annotation { "Feature Type Name" : "Feature", "Feature Type Description" : "" }
export const myFeature = defineFeature(function(context is Context, id is Id, definition is map)
    precondition{}
    {
        {
            var Q0;
            Q0=qCreatedBy(makeId("Front.planeOp"),FACE);
            var sketch = newSketch(context, id + "F0", { "sketchPlane" : qUnion([Q0])});
            skLineSegment(sketch, "E0.bottom", {"start": v(-37.24, 68.03) * mm, "end": v(38.96, 68.03) * mm});
            skLineSegment(sketch, "E0.top", {"start": v(-37.24, -46.27) * mm, "end": v(38.96, -46.27) * mm});
            skLineSegment(sketch, "E0.left", {"start": v(-37.24, 68.03) * mm, "end": v(-37.24, -46.27) * mm});
            skLineSegment(sketch, "E0.right", {"start": v(38.96, 68.03) * mm, "end": v(38.96, -46.27) * mm});
            skCircle(sketch, "E1", {"center": v(0, 61.6) * mm, "radius": 3.18 * mm});
            skSolve(sketch);
        }
        {
            var Q0;
            Q0 = qSketchRegion(id + "F0", true);
            extrude(context, id + "F1", {"entities" : qUnion([Q0]), "depth" : 3.17 * mm});
        }
        {
            var Q0;
            Q0=makeQuery(id+"F1.opExtrude","CAP_FACE",FACE,{"disambiguationData":[OSD([sQuery(id+"F0.wireOp",EDGE,"E0.bottom"),sQuery(id+"F0.wireOp",EDGE,"E0.top"),sQuery(id+"F0.wireOp",EDGE,"E0.left"),sQuery(id+"F0.wireOp",EDGE,"E0.right"),sQuery(id+"F0.wireOp",EDGE,"E1")])],"isStart":false});
            var sketch = newSketch(context, id + "F2", { "sketchPlane" : qUnion([Q0])});
            skFitSpline(sketch, "E2", {"points": [v(-30.48, 53.63) * mm, v(-30.48, 53.13) * mm, v(-30.48, 52.34) * mm, v(-30.48, 51.78) * mm, v(-30.67, 51.78) * mm, v(-30.99, 51.82) * mm, v(-31.3, 51.64) * mm, v(-31.49, 51.22) * mm, v(-31.19, 50.58) * mm, v(-30.8, 49.83) * mm, v(-30.6, 49.33) * mm, v(-30.63, 48.52) * mm, v(-30.91, 47.8) * mm, v(-31.24, 47.37) * mm, v(-31.82, 46.99) * mm, v(-32.55, 46.7) * mm, v(-33.63, 46.7) * mm, v(-34.1, 46.85) * mm, v(-34.1, 47.29) * mm, v(-34.09, 48.21) * mm, v(-34.08, 48.74) * mm, v(-33.95, 48.76) * mm, v(-33.62, 48.7) * mm, v(-33.25, 48.76) * mm, v(-32.99, 49.03) * mm, v(-32.94, 49.35) * mm, v(-33.1, 49.69) * mm, v(-33.37, 50.18) * mm, v(-33.58, 50.72) * mm, v(-33.68, 51.1) * mm, v(-33.68, 51.82) * mm, v(-33.67, 52.05) * mm, v(-33.42, 52.52) * mm, v(-33.13, 52.96) * mm, v(-32.7, 53.36) * mm, v(-32.33, 53.64) * mm, v(-31.72, 53.79) * mm, v(-30.93, 53.8) * mm, v(-30.64, 53.75) * mm, v(-30.48, 53.63) * mm]});
            skLineSegment(sketch, "E3", {"start": v(-29.84, 53.68) * mm, "end": v(-29.84, 51.83) * mm});
            skLineSegment(sketch, "E4", {"start": v(-29.84, 51.83) * mm, "end": v(-28.28, 51.83) * mm});
            skLineSegment(sketch, "E5", {"start": v(-28.28, 51.83) * mm, "end": v(-28.28, 46.75) * mm});
            skLineSegment(sketch, "E6", {"start": v(-28.28, 46.75) * mm, "end": v(-26.17, 46.75) * mm});
            skLineSegment(sketch, "E7", {"start": v(-26.17, 46.75) * mm, "end": v(-26.17, 51.71) * mm});
            skLineSegment(sketch, "E8", {"start": v(-24.73, 53.66) * mm, "end": v(-29.84, 53.68) * mm});
            skLineSegment(sketch, "E9", {"start": v(-26.17, 51.71) * mm, "end": v(-26.17, 51.83) * mm});
            skLineSegment(sketch, "E10", {"start": v(-26.17, 51.83) * mm, "end": v(-24.73, 51.83) * mm});
            skLineSegment(sketch, "E11", {"start": v(-24.73, 51.83) * mm, "end": v(-24.73, 53.66) * mm});
            skLineSegment(sketch, "E12", {"start": v(-19.94, 53.7) * mm, "end": v(-19.94, 51.85) * mm});
            skLineSegment(sketch, "E13", {"start": v(-19.94, 51.85) * mm, "end": v(-21.4, 51.85) * mm});
            skLineSegment(sketch, "E14", {"start": v(-21.43, 50.99) * mm, "end": v(-20.1, 50.99) * mm});
            skLineSegment(sketch, "E15", {"start": v(-20.1, 50.99) * mm, "end": v(-20.1, 49.46) * mm});
            skLineSegment(sketch, "E16", {"start": v(-20.1, 49.46) * mm, "end": v(-21.51, 49.46) * mm});
            skLineSegment(sketch, "E17", {"start": v(-21.56, 48.73) * mm, "end": v(-19.94, 48.73) * mm});
            skLineSegment(sketch, "E18", {"start": v(-19.94, 48.73) * mm, "end": v(-19.94, 46.85) * mm});
            skLineSegment(sketch, "E19", {"start": v(-19.94, 46.85) * mm, "end": v(-21.85, 46.85) * mm});
            skLineSegment(sketch, "E20", {"start": v(-19.94, 53.7) * mm, "end": v(-22.07, 53.7) * mm});
            skFitSpline(sketch, "E21", {"points": [v(-22.07, 53.7) * mm, v(-22.34, 53.7) * mm, v(-22.9, 53.47) * mm, v(-23.57, 52.9) * mm, v(-23.85, 52.37) * mm], "startDerivative": vector(-1.48, 0.16) * mm, "endDerivative": vector(-0.8, -2.12) * mm});
            skLineSegment(sketch, "E22", {"start": v(-23.85, 52.37) * mm, "end": v(-23.85, 50.44) * mm});
            skLineSegment(sketch, "E23", {"start": v(-23.85, 50.44) * mm, "end": v(-23.85, 48.3) * mm});
            skFitSpline(sketch, "E24", {"points": [v(-23.85, 48.3) * mm, v(-23.85, 48.05) * mm, v(-23.57, 47.64) * mm, v(-23.22, 47.24) * mm, v(-22.66, 46.9) * mm, v(-21.85, 46.85) * mm], "startDerivative": vector(-0.3, -1.73) * mm, "endDerivative": vector(3.43, 0.14) * mm});
            skLineSegment(sketch, "E25", {"start": v(-22.13, 46.84) * mm, "end": v(-21.85, 46.85) * mm});
            skFitSpline(sketch, "E26", {"points": [v(-21.51, 49.46) * mm, v(-21.7, 49.46) * mm, v(-21.83, 49.33) * mm, v(-21.93, 49.12) * mm, v(-21.8, 48.83) * mm, v(-21.56, 48.73) * mm], "startDerivative": vector(-1.07, 0.16) * mm, "endDerivative": vector(1.22, -0.29) * mm});
            skFitSpline(sketch, "E27", {"points": [v(-21.4, 51.85) * mm, v(-21.56, 51.8) * mm, v(-21.71, 51.73) * mm, v(-21.76, 51.6) * mm, v(-21.78, 51.37) * mm, v(-21.7, 51.2) * mm, v(-21.43, 50.99) * mm], "startDerivative": vector(-1, -0.32) * mm, "endDerivative": vector(1.5, -0.9) * mm});
            skLineSegment(sketch, "E28", {"start": v(-16.5, 51.46) * mm, "end": v(-16.5, 46.84) * mm});
            skLineSegment(sketch, "E29", {"start": v(-16.5, 46.84) * mm, "end": v(-18.54, 46.84) * mm});
            skLineSegment(sketch, "E30", {"start": v(-18.54, 46.84) * mm, "end": v(-18.54, 52.29) * mm});
            skLineSegment(sketch, "E31", {"start": v(-15.91, 51.49) * mm, "end": v(-15.91, 46.86) * mm});
            skLineSegment(sketch, "E32", {"start": v(-15.91, 46.86) * mm, "end": v(-13.89, 46.86) * mm});
            skLineSegment(sketch, "E33", {"start": v(-13.89, 46.86) * mm, "end": v(-13.89, 51.45) * mm});
            skPoint(sketch, "E34.start.orphan", {"position": v(-13.3, 51.45) * mm});
            skLineSegment(sketch, "E35", {"start": v(-13.3, 51.45) * mm, "end": v(-13.3, 46.84) * mm});
            skLineSegment(sketch, "E36", {"start": v(-13.3, 46.84) * mm, "end": v(-11.2, 46.84) * mm});
            skLineSegment(sketch, "E37", {"start": v(-11.2, 46.84) * mm, "end": v(-11.2, 52.1) * mm});
            skFitSpline(sketch, "E38", {"points": [v(-16.5, 51.46) * mm, v(-16.41, 51.6) * mm, v(-16.28, 51.7) * mm, v(-16.1, 51.66) * mm, v(-15.91, 51.49) * mm], "startDerivative": vector(0.3, 0.62) * mm, "endDerivative": vector(0.58, -0.71) * mm});
            skFitSpline(sketch, "E39", {"points": [v(-13.89, 51.45) * mm, v(-13.78, 51.6) * mm, v(-13.66, 51.73) * mm, v(-13.46, 51.7) * mm, v(-13.3, 51.45) * mm], "startDerivative": vector(0.44, 0.67) * mm, "endDerivative": vector(0.48, -0.99) * mm});
            skFitSpline(sketch, "E40", {"points": [v(-18.54, 52.29) * mm, v(-18.54, 52.5) * mm, v(-18.37, 52.81) * mm, v(-18.05, 53.24) * mm, v(-17.56, 53.61) * mm, v(-16.95, 53.81) * mm, v(-16.2, 53.8) * mm, v(-15.26, 53.38) * mm, v(-14.93, 53.04) * mm, v(-14.63, 53.28) * mm, v(-14.24, 53.58) * mm, v(-13.63, 53.8) * mm, v(-12.9, 53.83) * mm, v(-12.14, 53.55) * mm, v(-11.7, 53.19) * mm, v(-11.34, 52.63) * mm, v(-11.2, 52.1) * mm], "startDerivative": vector(-0.69, 5.32) * mm, "endDerivative": vector(1.48, -8.56) * mm});
            skLineSegment(sketch, "E41", {"start": v(-7.27, 51.88) * mm, "end": v(-7.27, 49.15) * mm});
            skLineSegment(sketch, "E42", {"start": v(-7.27, 49.15) * mm, "end": v(-7.27, 46.83) * mm});
            skLineSegment(sketch, "E43", {"start": v(-7.27, 46.83) * mm, "end": v(-5.22, 46.83) * mm});
            skLineSegment(sketch, "E44", {"start": v(-5.22, 46.83) * mm, "end": v(-5.22, 48.36) * mm});
            skLineSegment(sketch, "E45", {"start": v(-5.22, 48.36) * mm, "end": v(-4.7, 48.36) * mm});
            skLineSegment(sketch, "E46", {"start": v(-4.7, 48.36) * mm, "end": v(-4.7, 50.12) * mm});
            skLineSegment(sketch, "E47", {"start": v(-4.7, 50.12) * mm, "end": v(-5.18, 50.12) * mm});
            skLineSegment(sketch, "E48", {"start": v(-5.18, 50.12) * mm, "end": v(-5.18, 51.23) * mm});
            skLineSegment(sketch, "E49", {"start": v(-4.41, 51.45) * mm, "end": v(-4.41, 46.79) * mm});
            skLineSegment(sketch, "E50", {"start": v(-4.41, 46.79) * mm, "end": v(-2.3, 46.79) * mm});
            skLineSegment(sketch, "E51", {"start": v(-2.3, 46.79) * mm, "end": v(-2.3, 51.76) * mm});
            skFitSpline(sketch, "E52", {"points": [v(-5.18, 51.23) * mm, v(-5.18, 51.45) * mm, v(-5.06, 51.6) * mm, v(-4.88, 51.76) * mm, v(-4.62, 51.74) * mm, v(-4.41, 51.63) * mm, v(-4.41, 51.45) * mm], "startDerivative": vector(-0.2, 1.44) * mm, "endDerivative": vector(-0.28, -1.28) * mm});
            skPoint(sketch, "E53.1.internal.orphan", {"position": v(-7.27, 52.16) * mm});
            skFitSpline(sketch, "E54", {"points": [v(-7.27, 51.88) * mm, v(-7.27, 52.16) * mm, v(-7.15, 52.5) * mm, v(-6.93, 52.86) * mm, v(-6.15, 53.5) * mm, v(-5.36, 53.78) * mm, v(-4.25, 53.8) * mm, v(-3.38, 53.4) * mm, v(-2.7, 52.63) * mm, v(-2.3, 51.76) * mm], "startDerivative": vector(-0.36, 4) * mm, "endDerivative": vector(2.73, -7.06) * mm});
            skPoint(sketch, "E55.4.internal.orphan", {"position": v(1.88, 51.74) * mm});
            skPoint(sketch, "E55.5.internal.orphan", {"position": v(0.63, 51.74) * mm});
            skArc(sketch, "E56", {"start": v(3.7, 49.78) * mm, "mid": v(-1.39, 48.98) * mm, "end": v(3.75, 49.16) * mm});
            skArc(sketch, "E57", {"start": v(1.88, 49.76) * mm, "mid": v(0.41, 49.41) * mm, "end": v(1.89, 49.12) * mm});
            skLineSegment(sketch, "E58", {"start": v(1.88, 49.76) * mm, "end": v(3.7, 49.78) * mm});
            skLineSegment(sketch, "E59", {"start": v(3.75, 49.16) * mm, "end": v(1.89, 49.12) * mm});
            skArc(sketch, "E60", {"start": v(9.55, 49.88) * mm, "mid": v(4.75, 50.79) * mm, "end": v(7.47, 46.74) * mm});
            skArc(sketch, "E61", {"start": v(7.63, 49.41) * mm, "mid": v(6.22, 49.35) * mm, "end": v(7.39, 48.55) * mm});
            skLineSegment(sketch, "E62", {"start": v(7.39, 48.55) * mm, "end": v(7.47, 46.74) * mm});
            skLineSegment(sketch, "E63", {"start": v(7.63, 49.41) * mm, "end": v(7.63, 46.74) * mm});
            skLineSegment(sketch, "E64", {"start": v(7.63, 46.74) * mm, "end": v(9.63, 46.74) * mm});
            skLineSegment(sketch, "E65", {"start": v(9.63, 46.74) * mm, "end": v(9.55, 49.88) * mm});
            skArc(sketch, "E66", {"start": v(13.54, 51.72) * mm, "mid": v(11.07, 47.57) * mm, "end": v(15.72, 48.9) * mm});
            skArc(sketch, "E67", {"start": v(13.49, 49.87) * mm, "mid": v(12.42, 48.97) * mm, "end": v(13.81, 49.12) * mm});
            skLineSegment(sketch, "E68", {"start": v(13.54, 51.72) * mm, "end": v(13.49, 49.87) * mm});
            skLineSegment(sketch, "E69", {"start": v(13.81, 49.12) * mm, "end": v(13.81, 53.67) * mm});
            skLineSegment(sketch, "E70", {"start": v(13.81, 53.67) * mm, "end": v(15.69, 53.63) * mm});
            skLineSegment(sketch, "E71", {"start": v(15.69, 53.63) * mm, "end": v(15.72, 48.9) * mm});
            skArc(sketch, "E72", {"start": v(21.73, 49.02) * mm, "mid": v(16.83, 50.38) * mm, "end": v(20.85, 47.26) * mm});
            skLineSegment(sketch, "E73", {"start": v(21.73, 49.02) * mm, "end": v(18.9, 49.02) * mm});
            skLineSegment(sketch, "E74", {"start": v(18.9, 49.02) * mm, "end": v(18.9, 49.76) * mm});
            skLineSegment(sketch, "E75", {"start": v(18.9, 49.76) * mm, "end": v(19.95, 49.76) * mm});
            skLineSegment(sketch, "E76", {"start": v(19.79, 48.5) * mm, "end": v(20.85, 47.26) * mm});
            skFitSpline(sketch, "E77", {"points": [v(19.95, 49.76) * mm, v(19.89, 50.01) * mm, v(19.57, 50.33) * mm, v(19.06, 50.37) * mm, v(18.66, 49.93) * mm, v(18.51, 49.08) * mm, v(18.97, 48.39) * mm, v(19.79, 48.5) * mm], "startDerivative": vector(-0.3, 2.59) * mm, "endDerivative": vector(5.21, 1.83) * mm});
            skLineSegment(sketch, "E78", {"start": v(22.63, 50.3) * mm, "end": v(22.63, 46.84) * mm});
            skLineSegment(sketch, "E79", {"start": v(22.63, 46.84) * mm, "end": v(24.5, 46.84) * mm});
            skLineSegment(sketch, "E80", {"start": v(24.5, 46.84) * mm, "end": v(24.52, 49.49) * mm});
            skArc(sketch, "E81", {"start": v(26.01, 51.12) * mm, "mid": v(24.07, 51.77) * mm, "end": v(22.63, 50.3) * mm});
            skArc(sketch, "E82", {"start": v(29.36, 50.47) * mm, "mid": v(27.9, 51.87) * mm, "end": v(26.01, 51.12) * mm});
            skArc(sketch, "E83", {"start": v(25.08, 49.49) * mm, "mid": v(24.8, 49.9) * mm, "end": v(24.52, 49.49) * mm});
            skArc(sketch, "E84", {"start": v(27.62, 49.49) * mm, "mid": v(27.4, 49.85) * mm, "end": v(27.03, 49.63) * mm});
            skLineSegment(sketch, "E85", {"start": v(25.08, 49.49) * mm, "end": v(25.08, 46.84) * mm});
            skLineSegment(sketch, "E86", {"start": v(25.08, 46.84) * mm, "end": v(27.05, 46.84) * mm});
            skLineSegment(sketch, "E87", {"start": v(27.05, 46.84) * mm, "end": v(27.03, 49.63) * mm});
            skLineSegment(sketch, "E88", {"start": v(29.36, 50.47) * mm, "end": v(29.36, 46.8) * mm});
            skLineSegment(sketch, "E89", {"start": v(29.36, 46.8) * mm, "end": v(27.62, 46.8) * mm});
            skLineSegment(sketch, "E90", {"start": v(27.62, 46.8) * mm, "end": v(27.62, 49.49) * mm});
            skLineSegment(sketch, "E91", {"start": v(30.72, 51.75) * mm, "end": v(32.56, 51.75) * mm});
            skLineSegment(sketch, "E92", {"start": v(32.56, 51.75) * mm, "end": v(32.61, 48.97) * mm});
            skLineSegment(sketch, "E93", {"start": v(30.72, 51.75) * mm, "end": v(30.72, 48.15) * mm});
            skLineSegment(sketch, "E94", {"start": v(33.36, 48.9) * mm, "end": v(33.36, 51.73) * mm});
            skLineSegment(sketch, "E95", {"start": v(33.36, 51.73) * mm, "end": v(35.13, 51.73) * mm});
            skLineSegment(sketch, "E96", {"start": v(35.13, 51.73) * mm, "end": v(35.13, 46.95) * mm});
            skLineSegment(sketch, "E97", {"start": v(31.48, 46.1) * mm, "end": v(31.48, 44.74) * mm});
            skLineSegment(sketch, "E98", {"start": v(31.48, 44.74) * mm, "end": v(31.48, 44.58) * mm});
            skArc(sketch, "E99", {"start": v(32.61, 48.97) * mm, "mid": v(32.95, 48.6) * mm, "end": v(33.36, 48.9) * mm});
            skArc(sketch, "E100", {"start": v(30.72, 48.15) * mm, "mid": v(31.76, 46.92) * mm, "end": v(33.36, 47.08) * mm});
            skFitSpline(sketch, "E101", {"points": [v(33.36, 47.08) * mm, v(33.14, 46.68) * mm, v(32.58, 46.18) * mm, v(32.01, 46.05) * mm, v(31.48, 46.1) * mm], "startDerivative": vector(-0.76, -1.75) * mm, "endDerivative": vector(-2.19, 0.34) * mm});
            skFitSpline(sketch, "E102", {"points": [v(35.13, 46.95) * mm, v(35.13, 46.37) * mm, v(34.85, 45.87) * mm, v(34.16, 45.09) * mm, v(33.65, 44.69) * mm, v(32.75, 44.44) * mm, v(31.48, 44.58) * mm], "startDerivative": vector(0.42, -4.32) * mm, "endDerivative": vector(-6.24, 1.17) * mm});
            skSolve(sketch);
        }
        {
            var Q0;
            Q0=makeQuery(id+"F2.imprint","IMPRINT",FACE,{"disambiguationData":[TD([[makeQuery(id+"F2.imprint","IMPRINT",EDGE,{"derivedFrom":sQuery(id+"F2.wireOp",EDGE,"E2")}),-1.0]])]});
            var Q1;
            Q1=makeQuery(id+"F2.imprint","IMPRINT",FACE,{"disambiguationData":[TD([[makeQuery(id+"F2.imprint","IMPRINT",EDGE,{"derivedFrom":sQuery(id+"F2.wireOp",EDGE,"E3")}),1.0]])]});
            var Q2;
            Q2=makeQuery(id+"F2.imprint","IMPRINT",FACE,{"disambiguationData":[TD([[makeQuery(id+"F2.imprint","IMPRINT",EDGE,{"derivedFrom":sQuery(id+"F2.wireOp",EDGE,"E12")}),-1.0]])]});
            var Q3;
            Q3=makeQuery(id+"F2.imprint","IMPRINT",FACE,{"disambiguationData":[TD([[makeQuery(id+"F2.imprint","IMPRINT",EDGE,{"derivedFrom":sQuery(id+"F2.wireOp",EDGE,"E28")}),-1.0]])]});
            var Q4;
            Q4=makeQuery(id+"F2.imprint","IMPRINT",FACE,{"disambiguationData":[TD([[makeQuery(id+"F2.imprint","IMPRINT",EDGE,{"derivedFrom":sQuery(id+"F2.wireOp",EDGE,"E41")}),1.0]])]});
            var Q5;
            Q5=makeQuery(id+"F2.imprint","IMPRINT",FACE,{"disambiguationData":[TD([[makeQuery(id+"F2.imprint","IMPRINT",EDGE,{"derivedFrom":sQuery(id+"F2.wireOp",EDGE,"E56")}),1.0]])]});
            var Q6;
            Q6=makeQuery(id+"F2.imprint","IMPRINT",FACE,{"disambiguationData":[TD([[makeQuery(id+"F2.imprint","IMPRINT",EDGE,{"derivedFrom":sQuery(id+"F2.wireOp",EDGE,"E60")}),1.0]])]});
            var Q7;
            Q7=makeQuery(id+"F2.imprint","IMPRINT",FACE,{"disambiguationData":[TD([[makeQuery(id+"F2.imprint","IMPRINT",EDGE,{"derivedFrom":sQuery(id+"F2.wireOp",EDGE,"E66")}),1.0]])]});
            var Q8;
            Q8=makeQuery(id+"F2.imprint","IMPRINT",FACE,{"disambiguationData":[TD([[makeQuery(id+"F2.imprint","IMPRINT",EDGE,{"derivedFrom":sQuery(id+"F2.wireOp",EDGE,"E72")}),1.0]])]});
            var Q9;
            Q9=makeQuery(id+"F2.imprint","IMPRINT",FACE,{"disambiguationData":[TD([[makeQuery(id+"F2.imprint","IMPRINT",EDGE,{"derivedFrom":sQuery(id+"F2.wireOp",EDGE,"E78")}),1.0]])]});
            var Q10;
            Q10=makeQuery(id+"F2.imprint","IMPRINT",FACE,{"disambiguationData":[TD([[makeQuery(id+"F2.imprint","IMPRINT",EDGE,{"derivedFrom":sQuery(id+"F2.wireOp",EDGE,"E91")}),-1.0]])]});
            extrude(context, id + "F3", {"entities" : qUnion([Q0, Q1, Q2, Q3, Q4, Q5, Q6, Q7, Q8, Q9, Q10]), "operationType" : NewBodyOperationType.REMOVE, "oppositeDirection" : true, "depth" : 3.17 * mm});
        }
        {
            var Q0;
            Q0=makeQuery(id+"F1.opExtrude","CAP_FACE",FACE,{"disambiguationData":[OSD([sQuery(id+"F0.wireOp",EDGE,"E0.bottom"),sQuery(id+"F0.wireOp",EDGE,"E0.top"),sQuery(id+"F0.wireOp",EDGE,"E0.left"),sQuery(id+"F0.wireOp",EDGE,"E0.right"),sQuery(id+"F0.wireOp",EDGE,"E1")])],"isStart":false});
            var sketch = newSketch(context, id + "F4", { "sketchPlane" : qUnion([Q0])});
            skText(sketch, "E103", { "text": "Hall Pass", "fontName": "NotoSansCJKtc-Bold.otf"});
            const initialGuessF4  = {"E103": [-0.03423, 0.0326, 1, 0, 0.01078]};
            skSetInitialGuess(sketch, initialGuessF4);
            skSolve(sketch);
        }
        {
            var Q0;
            Q0 = qSketchRegion(id + "F4", true);
            extrude(context, id + "F5", {"entities" : qUnion([Q0]), "operationType" : NewBodyOperationType.REMOVE, "oppositeDirection" : true, "depth" : 25.4 * mm});
        }
        {
            var Q0;
            {var subQ0=sQuery(id+"F0.wireOp",EDGE,"E0.left");var subQ1=sQuery(id+"F0.wireOp",EDGE,"E0.top");var subQ2=sQuery(id+"F0.wireOp",EDGE,"E0.right");var subQ3=sQuery(id+"F0.wireOp",EDGE,"E1");var subQ4=sQuery(id+"F0.wireOp",EDGE,"E0.bottom");Q0=makeQuery(id+"F5.boolean.opBoolean","SPLIT",FACE,{"disambiguationData":[TD([makeQuery(id+"F1.opExtrude","SWEPT_FACE",FACE,{"disambiguationData":[OSD([subQ4])]})])],"derivedFrom":makeQuery(id+"F1.opExtrude","CAP_FACE",FACE,{"disambiguationData":[OSD([subQ4,subQ1,subQ0,subQ2,subQ3])],"isStart":false})});}
            var sketch = newSketch(context, id + "F6", { "sketchPlane" : qUnion([Q0])});
            skLineSegment(sketch, "E104", {"start": v(-10.04, 26.02) * mm, "end": v(-14.61, 18.29) * mm});
            skLineSegment(sketch, "E105", {"start": v(-14.61, 18.29) * mm, "end": v(-5.9, 12.73) * mm});
            skLineSegment(sketch, "E106", {"start": v(-5.9, 12.73) * mm, "end": v(0, 21.98) * mm});
            skLineSegment(sketch, "E107", {"start": v(-21.58, 12.4) * mm, "end": v(-11.56, 12.4) * mm});
            skLineSegment(sketch, "E108", {"start": v(-11.56, 12.4) * mm, "end": v(-6.88, 4.02) * mm});
            skLineSegment(sketch, "E109", {"start": v(-6.88, 4.02) * mm, "end": v(-9.27, 5.22) * mm});
            skLineSegment(sketch, "E110", {"start": v(-9.27, 5.22) * mm, "end": v(-13.3, -0.77) * mm});
            skLineSegment(sketch, "E111", {"start": v(-13.3, -0.77) * mm, "end": v(-14.5, -2.52) * mm});
            skLineSegment(sketch, "E112", {"start": v(-21.58, 12.4) * mm, "end": v(-18.75, 10.45) * mm});
            skLineSegment(sketch, "E113", {"start": v(-18.75, 10.45) * mm, "end": v(-21.83, 5.22) * mm});
            skLineSegment(sketch, "E114", {"start": v(-21.83, 5.22) * mm, "end": v(-21.83, 4.02) * mm});
            skLineSegment(sketch, "E115", {"start": v(-21.83, 4.02) * mm, "end": v(-15.7, -7.1) * mm});
            skFitSpline(sketch, "E116", {"points": [v(-14.5, -2.52) * mm, v(-15.2, -4.32) * mm, v(-15.7, -7.1) * mm], "startDerivative": vector(-1.7, -3.73) * mm, "endDerivative": vector(-0.73, -5.37) * mm});
            skPoint(sketch, "E117.3.internal.snap0", {"position": v(-2.95, 17.36) * mm});
            skFitSpline(sketch, "E117", {"points": [v(-10.04, 26.02) * mm, v(-8.51, 27.18) * mm, v(-5.9, 27.6) * mm, v(-2.95, 26.94) * mm, v(-1.25, 24) * mm, v(0, 21.98) * mm], "startDerivative": vector(8.08, 7.85) * mm, "endDerivative": vector(6.8, -9.49) * mm});
            skFitSpline(sketch, "E118", {"points": [v(-11.94, -1.05) * mm, v(-13, -2.52) * mm, v(-14.5, -5.22) * mm, v(-13.82, -8.8) * mm, v(-11.61, -11.1) * mm, v(-10.04, -11.74) * mm], "startDerivative": vector(-5.8, -8.2) * mm, "endDerivative": vector(9.47, -2.91) * mm});
            skLineSegment(sketch, "E119", {"start": v(-11.94, -1.05) * mm, "end": v(-1.09, -1.05) * mm});
            skLineSegment(sketch, "E120", {"start": v(-1.09, -1.05) * mm, "end": v(-1.03, -11.52) * mm});
            skLineSegment(sketch, "E121", {"start": v(-1.03, -11.52) * mm, "end": v(-10.04, -11.74) * mm});
            skLineSegment(sketch, "E122", {"start": v(13.38, -11.39) * mm, "end": v(7.27, -11.39) * mm});
            skLineSegment(sketch, "E123", {"start": v(7.27, -11.39) * mm, "end": v(7.27, -15.21) * mm});
            skLineSegment(sketch, "E124", {"start": v(7.27, -15.21) * mm, "end": v(1.99, -6.44) * mm});
            skLineSegment(sketch, "E125", {"start": v(1.99, -6.44) * mm, "end": v(7.14, 2.27) * mm});
            skLineSegment(sketch, "E126", {"start": v(7.14, 2.27) * mm, "end": v(7.14, -1.3) * mm});
            skLineSegment(sketch, "E127", {"start": v(7.14, -1.3) * mm, "end": v(18.4, -1.3) * mm});
            skFitSpline(sketch, "E128", {"points": [v(13.38, -11.39) * mm, v(14.62, -11.39) * mm, v(17.91, -5.28) * mm, v(20.66, -0.61) * mm, v(18.4, -1.3) * mm], "startDerivative": vector(8.55, -2.76) * mm, "endDerivative": vector(-15.5, -6.94) * mm});
            skPoint(sketch, "E129.0.internal.orphan", {"position": v(14.07, 0) * mm});
            skPoint(sketch, "E129.1.internal.orphan", {"position": v(18.4, 0) * mm});
            skFitSpline(sketch, "E130", {"points": [v(14.07, 0) * mm, v(17.3, 0) * mm, v(18.4, 0) * mm, v(20.72, 1.17) * mm, v(21.9, 2.48) * mm, v(22.54, 3.85) * mm, v(22.54, 4.88) * mm, v(22.54, 5.98) * mm, v(21.07, 8.93) * mm, v(17.77, 14.76) * mm], "startDerivative": vector(28.05, 0.63) * mm, "endDerivative": vector(-17.93, 32.26) * mm});
            skLineSegment(sketch, "E131", {"start": v(17.77, 14.76) * mm, "end": v(8.44, 9.75) * mm});
            skLineSegment(sketch, "E132", {"start": v(8.44, 9.75) * mm, "end": v(14.07, 0) * mm});
            skLineSegment(sketch, "E133", {"start": v(10.47, 27.39) * mm, "end": v(13.25, 22.2) * mm});
            skLineSegment(sketch, "E134", {"start": v(13.25, 22.2) * mm, "end": v(16.5, 23.93) * mm});
            skLineSegment(sketch, "E135", {"start": v(16.5, 23.93) * mm, "end": v(11.8, 14.76) * mm});
            skLineSegment(sketch, "E136", {"start": v(11.8, 14.76) * mm, "end": v(1.35, 15.27) * mm});
            skLineSegment(sketch, "E137", {"start": v(1.35, 15.27) * mm, "end": v(4.28, 16.84) * mm});
            skLineSegment(sketch, "E138", {"start": v(4.28, 16.84) * mm, "end": v(-0.82, 26.34) * mm});
            skLineSegment(sketch, "E139", {"start": v(-3.2, 28.18) * mm, "end": v(8.62, 28.18) * mm});
            skFitSpline(sketch, "E140", {"points": [v(-3.2, 28.18) * mm, v(-0.82, 26.34) * mm], "startDerivative": vector(2.4, -1.84) * mm, "endDerivative": vector(2.4, -1.84) * mm});
            skFitSpline(sketch, "E141", {"points": [v(8.62, 28.18) * mm, v(10.47, 27.39) * mm], "startDerivative": vector(1.85, -0.8) * mm, "endDerivative": vector(1.85, -0.8) * mm});
            skFitSpline(sketch, "E142", {"points": [v(-3.2, 28.18) * mm, v(-2.41, 27.57) * mm, v(-1.61, 26.96) * mm, v(-0.82, 26.34) * mm], "startDerivative": vector(2.4, -1.84) * mm, "endDerivative": vector(2.4, -1.84) * mm});
            skFitSpline(sketch, "E143", {"points": [v(8.62, 28.18) * mm, v(9.24, 27.91) * mm, v(9.85, 27.65) * mm, v(10.47, 27.39) * mm], "startDerivative": vector(1.85, -0.8) * mm, "endDerivative": vector(1.85, -0.8) * mm});
            skSolve(sketch);
        }
        {
            var Q0;
            Q0=makeQuery(id+"F6.imprint","IMPRINT",FACE,{"disambiguationData":[TD([[makeQuery(id+"F6.imprint","IMPRINT",EDGE,{"derivedFrom":sQuery(id+"F6.wireOp",EDGE,"E107")}),-1.0]])]});
            var Q1;
            Q1=makeQuery(id+"F6.imprint","IMPRINT",FACE,{"disambiguationData":[TD([[makeQuery(id+"F6.imprint","IMPRINT",EDGE,{"derivedFrom":sQuery(id+"F6.wireOp",EDGE,"E118")}),1.0]])]});
            var Q2;
            Q2=makeQuery(id+"F6.imprint","IMPRINT",FACE,{"disambiguationData":[TD([[makeQuery(id+"F6.imprint","IMPRINT",EDGE,{"derivedFrom":sQuery(id+"F6.wireOp",EDGE,"E122")}),-1.0]])]});
            var Q3;
            Q3=makeQuery(id+"F6.imprint","IMPRINT",FACE,{"disambiguationData":[TD([[makeQuery(id+"F6.imprint","IMPRINT",EDGE,{"derivedFrom":sQuery(id+"F6.wireOp",EDGE,"E130")}),1.0]])]});
            var Q4;
            Q4=makeQuery(id+"F6.imprint","IMPRINT",FACE,{"disambiguationData":[TD([[makeQuery(id+"F6.imprint","IMPRINT",EDGE,{"derivedFrom":sQuery(id+"F6.wireOp",EDGE,"E104")}),1.0]])]});
            var Q5;
            Q5=makeQuery(id+"F6.imprint","IMPRINT",FACE,{"disambiguationData":[TD([[makeQuery(id+"F6.imprint","IMPRINT",EDGE,{"derivedFrom":sQuery(id+"F6.wireOp",EDGE,"E133")}),-1.0]])]});
            extrude(context, id + "F7", {"entities" : qUnion([Q0, Q1, Q2, Q3, Q4, Q5]), "depth" : 3.17 * mm});
        }
        {
            var Q0;
            {var subQ0=sQuery(id+"F0.wireOp",EDGE,"E0.left");var subQ1=sQuery(id+"F0.wireOp",EDGE,"E0.top");var subQ2=sQuery(id+"F0.wireOp",EDGE,"E0.right");var subQ3=sQuery(id+"F0.wireOp",EDGE,"E1");var subQ4=sQuery(id+"F0.wireOp",EDGE,"E0.bottom");Q0=makeQuery(id+"F5.boolean.opBoolean","SPLIT",FACE,{"disambiguationData":[TD([makeQuery(id+"F1.opExtrude","SWEPT_FACE",FACE,{"disambiguationData":[OSD([subQ4])]})])],"derivedFrom":makeQuery(id+"F1.opExtrude","CAP_FACE",FACE,{"disambiguationData":[OSD([subQ4,subQ1,subQ0,subQ2,subQ3])],"isStart":false})});}
            var sketch = newSketch(context, id + "F8", { "sketchPlane" : qUnion([Q0])});
            skCircle(sketch, "E144", {"center": v(28.78, -20.57) * mm, "radius": 2.12 * mm});
            skLineSegment(sketch, "E145", {"start": v(20.05, -22.9) * mm, "end": v(30.82, -22.9) * mm});
            skLineSegment(sketch, "E146", {"start": v(20.05, -22.9) * mm, "end": v(26.91, -25.07) * mm});
            skLineSegment(sketch, "E147", {"start": v(33.45, -28.56) * mm, "end": v(28.86, -28.9) * mm});
            skLineSegment(sketch, "E148", {"start": v(28.86, -28.9) * mm, "end": v(33.45, -28.9) * mm});
            skLineSegment(sketch, "E149", {"start": v(33.45, -28.9) * mm, "end": v(32.37, -41.02) * mm});
            skLineSegment(sketch, "E150", {"start": v(32.37, -41.02) * mm, "end": v(30.32, -33.62) * mm});
            skLineSegment(sketch, "E151", {"start": v(30.32, -33.62) * mm, "end": v(26.1, -40.98) * mm});
            skLineSegment(sketch, "E152", {"start": v(26.1, -40.98) * mm, "end": v(27.98, -28.73) * mm});
            skFitSpline(sketch, "E153", {"points": [v(26.91, -25.07) * mm, v(27.23, -25.93) * mm, v(27.52, -26.8) * mm, v(27.77, -28.06) * mm, v(27.98, -28.73) * mm], "startDerivative": vector(1.28, -3.54) * mm, "endDerivative": vector(1.01, -2.78) * mm});
            skFitSpline(sketch, "E154", {"points": [v(30.82, -22.9) * mm, v(31.36, -23.38) * mm, v(31.87, -24.22) * mm, v(32.33, -25.07) * mm, v(32.83, -26.35) * mm, v(33.12, -27.23) * mm, v(33.45, -28.56) * mm], "startDerivative": vector(4.11, -3.02) * mm, "endDerivative": vector(1.76, -7.5) * mm});
            skLineSegment(sketch, "E155", {"start": v(16.69, -30.26) * mm, "end": v(18.66, -40.68) * mm});
            skLineSegment(sketch, "E156", {"start": v(18.66, -40.68) * mm, "end": v(23.98, -40.68) * mm});
            skLineSegment(sketch, "E157", {"start": v(23.98, -40.68) * mm, "end": v(25.14, -30.41) * mm});
            skArc(sketch, "E158", {"start": v(16.6, -29.47) * mm, "mid": v(16.21, -29.91) * mm, "end": v(16.69, -30.26) * mm});
            skArc(sketch, "E159", {"start": v(25.14, -30.41) * mm, "mid": v(25.58, -29.96) * mm, "end": v(25.14, -29.5) * mm});
            skLineSegment(sketch, "E160", {"start": v(16.6, -29.47) * mm, "end": v(25.14, -29.5) * mm});
            skLineSegment(sketch, "E161", {"start": v(20.06, -25.33) * mm, "end": v(21.37, -25.86) * mm});
            skFitSpline(sketch, "E162", {"points": [v(21.37, -25.86) * mm, v(21.88, -25.86) * mm, v(22.52, -25.66) * mm, v(23.2, -25.28) * mm, v(23.45, -25.13) * mm, v(23.7, -25.26) * mm, v(23.65, -25.6) * mm, v(24, -26.1) * mm, v(24.31, -26.1) * mm, v(24.58, -26.08) * mm, v(24.73, -26.32) * mm, v(24.05, -26.92) * mm, v(23.4, -27.52) * mm, v(22.8, -28.27) * mm, v(22.8, -28.54) * mm, v(22.8, -28.78) * mm, v(22.45, -28.78) * mm, v(21.99, -28.6) * mm, v(20.97, -28.74) * mm, v(19.75, -28.9) * mm, v(18.73, -28.76) * mm, v(17.82, -27.98) * mm, v(18.07, -27.7) * mm, v(18.98, -27.03) * mm, v(19.62, -26.2) * mm, v(19.73, -25.86) * mm, v(20.06, -25.33) * mm], "startDerivative": vector(14.04, -0.97) * mm, "endDerivative": vector(10.18, 14.4) * mm});
            skSolve(sketch);
        }
        {
            var Q0;
            Q0=makeQuery(id+"F8.imprint","IMPRINT",FACE,{"disambiguationData":[TD([[makeQuery(id+"F8.imprint","IMPRINT",EDGE,{"derivedFrom":sQuery(id+"F8.wireOp",EDGE,"E144")}),1.0]])]});
            var Q1;
            Q1=makeQuery(id+"F8.imprint","IMPRINT",FACE,{"disambiguationData":[TD([[makeQuery(id+"F8.imprint","IMPRINT",EDGE,{"derivedFrom":sQuery(id+"F8.wireOp",EDGE,"E155")}),1.0]])]});
            var Q2;
            Q2=makeQuery(id+"F8.imprint","IMPRINT",FACE,{"disambiguationData":[TD([[makeQuery(id+"F8.imprint","IMPRINT",EDGE,{"derivedFrom":sQuery(id+"F8.wireOp",EDGE,"E161")}),-1.0]])]});
            var Q3;
            Q3=makeQuery(id+"F8.imprint","IMPRINT",FACE,{"disambiguationData":[TD([[makeQuery(id+"F8.imprint","IMPRINT",EDGE,{"derivedFrom":sQuery(id+"F8.wireOp",EDGE,"E145")}),-1.0]])]});
            extrude(context, id + "F9", {"entities" : qUnion([Q0, Q1, Q2, Q3]), "operationType" : NewBodyOperationType.REMOVE, "oppositeDirection" : true, "depth" : 25.4 * mm});
        }
        {
            var Q0;
            {var subQ0=sQuery(id+"F0.wireOp",EDGE,"E0.left");var subQ1=sQuery(id+"F0.wireOp",EDGE,"E0.top");var subQ2=sQuery(id+"F0.wireOp",EDGE,"E0.right");var subQ3=sQuery(id+"F0.wireOp",EDGE,"E1");var subQ4=sQuery(id+"F0.wireOp",EDGE,"E0.bottom");Q0=makeQuery(id+"F5.boolean.opBoolean","SPLIT",FACE,{"disambiguationData":[TD([makeQuery(id+"F1.opExtrude","SWEPT_FACE",FACE,{"disambiguationData":[OSD([subQ4])]})])],"derivedFrom":makeQuery(id+"F1.opExtrude","CAP_FACE",FACE,{"disambiguationData":[OSD([subQ4,subQ1,subQ0,subQ2,subQ3])],"isStart":false})});}
            var sketch = newSketch(context, id + "F10", { "sketchPlane" : qUnion([Q0])});
            skText(sketch, "E163", { "text": "Go green or \ngo home!", "fontName": "AllertaStencil-Regular.ttf"});
            const initialGuessF10  = {"E163": [-0.0352, -0.02718, 1, 0, 0.0061]};
            skSetInitialGuess(sketch, initialGuessF10);
            skSolve(sketch);
        }
        {
            var Q0;
            Q0 = qSketchRegion(id + "F10", true);
            extrude(context, id + "F11", {"entities" : qUnion([Q0]), "operationType" : NewBodyOperationType.REMOVE, "oppositeDirection" : true, "depth" : 25.4 * mm});
        }
    });